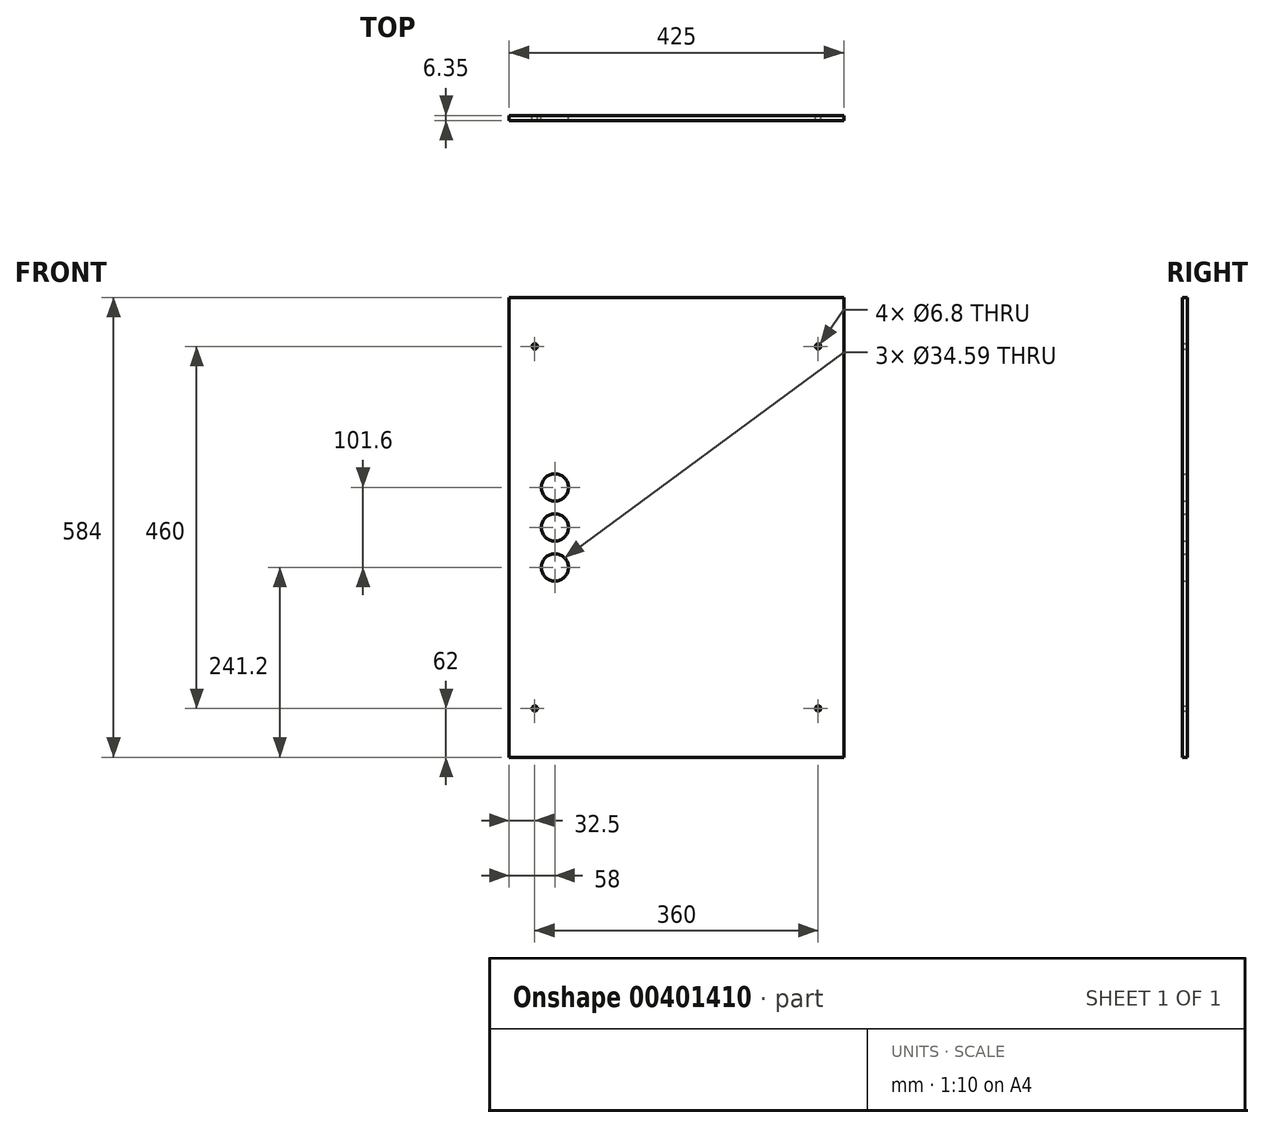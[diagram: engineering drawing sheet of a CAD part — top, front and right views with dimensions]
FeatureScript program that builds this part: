
annotation { "Feature Type Name" : "Feature", "Feature Type Description" : "" }
export const myFeature = defineFeature(function(context is Context, id is Id, definition is map)
    precondition{}
    {
        {
            var Q0;
            Q0=qCreatedBy(makeId("Front.planeOp"),FACE);
            var sketch = newSketch(context, id + "F0", { "sketchPlane" : qUnion([Q0])});
            skLineSegment(sketch, "E0.bottom", {"start": v(212.5, -292) * mm, "end": v(-212.5, -292) * mm});
            skLineSegment(sketch, "E0.top", {"start": v(212.5, 292) * mm, "end": v(-212.5, 292) * mm});
            skLineSegment(sketch, "E0.left", {"start": v(212.5, -292) * mm, "end": v(212.5, 292) * mm});
            skLineSegment(sketch, "E0.right", {"start": v(-212.5, -292) * mm, "end": v(-212.5, 292) * mm});
            skPoint(sketch, "E0.middle", {"position": v(0, 0) * mm});
            skPoint(sketch, "E1", {"position": v(-180, 230) * mm});
            skPoint(sketch, "E2", {"position": v(180, 230) * mm});
            skPoint(sketch, "E3", {"position": v(180, -230) * mm});
            skPoint(sketch, "E4", {"position": v(-180, -230) * mm});
            skPoint(sketch, "E5", {"position": v(-154.5, -50.8) * mm});
            skPoint(sketch, "E6", {"position": v(-154.5, 0) * mm});
            skPoint(sketch, "E7", {"position": v(-154.5, 50.8) * mm});
            skLineSegment(sketch, "E8.bottom", {"start": v(200, -250) * mm, "end": v(-200, -250) * mm, "construction": true});
            skLineSegment(sketch, "E8.top", {"start": v(200, 250) * mm, "end": v(-200, 250) * mm, "construction": true});
            skLineSegment(sketch, "E8.left", {"start": v(200, -250) * mm, "end": v(200, 250) * mm, "construction": true});
            skLineSegment(sketch, "E8.right", {"start": v(-200, -250) * mm, "end": v(-200, 250) * mm, "construction": true});
            skLineSegment(sketch, "E9", {"start": v(-180, 230) * mm, "end": v(180, -230) * mm, "construction": true});
            skLineSegment(sketch, "E10", {"start": v(-180, -230) * mm, "end": v(180, 230) * mm, "construction": true});
            skCircle(sketch, "E11", {"center": v(-154.5, 50.8) * mm, "radius": 17.3 * mm, "construction": true});
            skCircle(sketch, "E12", {"center": v(-154.5, 0) * mm, "radius": 17.3 * mm, "construction": true});
            skCircle(sketch, "E13", {"center": v(-154.5, -50.8) * mm, "radius": 17.3 * mm, "construction": true});
            skCircle(sketch, "E14", {"center": v(-180, -230) * mm, "radius": 3.4 * mm, "construction": true});
            skCircle(sketch, "E15", {"center": v(180, 230) * mm, "radius": 3.4 * mm, "construction": true});
            skCircle(sketch, "E16", {"center": v(-180, 230) * mm, "radius": 3.4 * mm, "construction": true});
            skCircle(sketch, "E17", {"center": v(180, -230) * mm, "radius": 3.4 * mm, "construction": true});
            skSolve(sketch);
        }
        {
            var Q0;
            Q0=makeQuery(id+"F0.imprint","IMPRINT",FACE,{"disambiguationData":[TD([[makeQuery(id+"F0.imprint","IMPRINT",EDGE,{"derivedFrom":sQuery(id+"F0.wireOp",EDGE,"E0.bottom")}),-1.0]])]});
            extrude(context, id + "F1", {"entities" : qUnion([Q0]), "depth" : 6.35 * mm});
        }
        {
            var Q0;
            Q0=sQuery(id+"F0.wireOp",VERTEX,"E1");
            var Q1;
            Q1=sQuery(id+"F0.wireOp",VERTEX,"E4");
            var Q2;
            Q2=sQuery(id+"F0.wireOp",VERTEX,"E3");
            var Q3;
            Q3=sQuery(id+"F0.wireOp",VERTEX,"E2");
            var Q4;
            Q4=makeQuery(id+"F1.opExtrude","SWEPT_BODY",BODY,{"disambiguationData":[OSD([sQuery(id+"F0.wireOp",EDGE,"E0.bottom"),sQuery(id+"F0.wireOp",EDGE,"E0.top"),sQuery(id+"F0.wireOp",EDGE,"E0.left"),sQuery(id+"F0.wireOp",EDGE,"E0.right")])]});
            hole(context, id + "F2", {"style" : HoleStyle.SIMPLE, "endStyle" : HoleEndStyle.THROUGH, "oppositeDirection" : true, "standardTappedOrClearance" : lookupTablePath({ "standard" : "ISO", "engagement" : "75%", "pitch" : "1.25 mm", "size" : "M8", "type" : "Tapped" }), "standardBlindInLast" : lookupTablePath({ "standard" : "ISO", "engagement" : "75%", "pitch" : "1.25 mm", "size" : "M8", "type" : "Tapped" }), "holeDiameter" : 6.8 * mm, "showTappedDepth" : true, "isTappedThrough" : true, "tappedDepth" : 12 * mm, "tapClearance" : 3, "locations" : qUnion([Q0, Q1, Q2, Q3]), "scope" : qUnion([Q4]), "majorDiameter" : 8 * mm});
        }
        {
            var Q0;
            Q0=sQuery(id+"F0.wireOp",VERTEX,"E7");
            var Q1;
            Q1=sQuery(id+"F0.wireOp",VERTEX,"E6");
            var Q2;
            Q2=sQuery(id+"F0.wireOp",VERTEX,"E5");
            var Q3;
            Q3=makeQuery(id+"F1.opExtrude","SWEPT_BODY",BODY,{"disambiguationData":[OSD([sQuery(id+"F0.wireOp",EDGE,"E0.bottom"),sQuery(id+"F0.wireOp",EDGE,"E0.top"),sQuery(id+"F0.wireOp",EDGE,"E0.left"),sQuery(id+"F0.wireOp",EDGE,"E0.right")])]});
            hole(context, id + "F3", {"style" : HoleStyle.SIMPLE, "endStyle" : HoleEndStyle.THROUGH, "oppositeDirection" : true, "holeDiameter" : 34.6 * mm, "isTappedThrough" : true, "tappedDepth" : 12 * mm, "tapClearance" : 3, "locations" : qUnion([Q0, Q1, Q2]), "scope" : qUnion([Q3])});
        }
    });
